# Revit family: LUXI_DOWNLIGHT_OD-E
name_source: partatom
category: Apparecchi per illuminazione
revit_build: Autodesk Revit 2016 (Build: 20161004_0715(x64)
units: mm (PartAtom-declared; Revit-internal decimal feet)

## family parameters
Condiviso = No
Host = Superficie
Numero OmniClass = 23.80.70.00
Punto di calcolo locali = Sì
Quota connettore circolare = Usa diametro
Sorgente d'illuminazione = Sì
Taglio con vuoti quando caricato = No
Tipo di parte = Normale
Titolo OmniClass = Lighting

## types (8) — shared parameters
ANG1 = 50.00°
Angolo inclinazione = -90.00°
CRI = ≥80 (typ.)
Certifications = CE / RohS
Color = White
Descrizione = LED Downlight with integrated driver
Dust and water protection rating = IP 44 (front)
Energy class = A+
Ext. thickness = 2 mm  [stored 0.00656168 ft]
Filtro dei colori = 16777215
IFCExportAs = IfcLightFixtureType
Impact rating = IK06 (1 Joule)
Installation = Recessed
Lifetime = L70B50 30.000h
Light distribution = Downlight
Light source = LED SMD
Masterformat 2016 code = 26.50.00
Masterformat 2016 description = Lighting
Material 1 = Polycarbonate_White
Material 2 = Opal Technopolimer
Modello = OD-E Series | Downlight
Operating temperature = 0°C / +40°C
Optics = Metalized reflector, opal diffusing panel
Photobiological risk group = RG0
Power factor = ≥0,90 (typ.)
Power supply = Included, not dimmable
Produttore = Luxi Illuminazione S.r.l.
Prospetto di default = 2000 mm  [stored 6.56168 ft]
Protection class = II
Rated supply voltage = 220-240V AC / 50-60 Hz
Rendi la forma visibile nel rendering = No
Review = 3
Step MacAdam (SDCM) = <4
URL = https://www.luxi.lighting
Uniclass 2015 code = EF_70_80
Uniclass 2015 description = Lighting
Variazione temperatura colore lampada con luminosità attenuata = <Nessuno>
Warranty = 3 years

## per-type parameters (varying)
| type | Carico apparente | Code | Diameter | Emetti da diametro cerchio | File diagramma fotometrico | H | H_mid | H_quart | OFF1 | OFF2 | OFF3 | OFF4 | Recession | Size | Wattage | Weight |
| DLDE010100W830 | 10 VA | DLDE010100W830 | 113 mm  [stored 0.370735 ft] | 100 mm  [stored 0.328084 ft] | DLDE010100W830 Luxi Serie OD-E 10W 3000K.IES | 59 mm | 30 mm  [stored 0.0984252 ft] | 15 mm | 25 mm  [stored 0.082021 ft] | 10 mm  [stored 0.0328084 ft] | 7 mm  [stored 0.0229659 ft] | 7 mm  [stored 0.0229659 ft] | 100 mm  [stored 0.328084 ft] | Ø113x59 recession Ø100 | 10 W | 0.30 kg |
| DLDE010100W840 | 10 VA | DLDE010100W840 | 113 mm  [stored 0.370735 ft] | 100 mm  [stored 0.328084 ft] | DLDE010100W840 Luxi Serie OD-E 10W 4000K.IES | 59 mm | 30 mm  [stored 0.0984252 ft] | 15 mm | 25 mm  [stored 0.082021 ft] | 10 mm  [stored 0.0328084 ft] | 7 mm  [stored 0.0229659 ft] | 7 mm  [stored 0.0229659 ft] | 100 mm  [stored 0.328084 ft] | Ø113x59 recession Ø100 | 10 W | 0.30 kg |
| DLDE017150W830 | 17 VA | DLDE017150W830 | 174 mm  [stored 0.570866 ft] | 150 mm  [stored 0.492126 ft] | DLDE017150W830 Luxi Serie OD-E 17W 3000K.IES | 66 mm  [stored 0.216535 ft] | 33 mm  [stored 0.108268 ft] | 17 mm | 28 mm | 11 mm | 8 mm  [stored 0.0262467 ft] | 12 mm  [stored 0.0393701 ft] | 150 mm  [stored 0.492126 ft] | Ø174x66 recession Ø150 | 17 W | 0.30 kg |
| DLDE017150W840 | 17 VA | DLDE017150W830 | 174 mm  [stored 0.570866 ft] | 150 mm  [stored 0.492126 ft] | DLDE017150W840 Luxi Serie OD-E 17W 4000K.IES | 66 mm  [stored 0.216535 ft] | 33 mm  [stored 0.108268 ft] | 17 mm | 28 mm | 11 mm | 8 mm  [stored 0.0262467 ft] | 12 mm  [stored 0.0393701 ft] | 150 mm  [stored 0.492126 ft] | Ø174x66 recession Ø150 | 17 W | 0.30 kg |
| DLDE025200W830 | 25 VA | DLDE025200W830 | 224 mm  [stored 0.734908 ft] | 200 mm  [stored 0.656168 ft] | DLDE025200W830 Luxi Serie OD-E 25W 3000K.IES | 85 mm  [stored 0.278871 ft] | 43 mm | 21 mm | 36 mm | 14 mm  [stored 0.0459318 ft] | 11 mm | 12 mm  [stored 0.0393701 ft] | 200 mm  [stored 0.656168 ft] | Ø224x85 recession Ø200 | 25 W | 0.50 kg |
| DLDE025200W840 | 25 VA | DLDE025200W840 | 224 mm  [stored 0.734908 ft] | 200 mm  [stored 0.656168 ft] | DLDE025200W840 Luxi Serie OD-E 25W 4000K.IES | 85 mm  [stored 0.278871 ft] | 43 mm | 21 mm | 36 mm | 14 mm  [stored 0.0459318 ft] | 11 mm | 12 mm  [stored 0.0393701 ft] | 200 mm  [stored 0.656168 ft] | Ø224x85 recession Ø200 | 25 W | 0.50 kg |
| DLDE035240W830 | 35 VA | DLDE035240W830 | 279 mm | 240 mm  [stored 0.787402 ft] | DLDE035240W830 Luxi Serie OD-E 35W 3000K.IES | 119 mm  [stored 0.39042 ft] | 60 mm | 30 mm  [stored 0.0984252 ft] | 50 mm  [stored 0.164042 ft] | 20 mm | 15 mm | 20 mm | 240 mm  [stored 0.787402 ft] | Ø279x119 recession Ø240 | 35 W | 0.60 kg |
| DLDE035240W840 | 35 VA | DLDE035240W840 | 279 mm | 240 mm  [stored 0.787402 ft] | DLDE035240W840 Luxi Serie OD-E 35W 4000K.IES | 119 mm  [stored 0.39042 ft] | 60 mm | 30 mm  [stored 0.0984252 ft] | 50 mm  [stored 0.164042 ft] | 20 mm | 15 mm | 20 mm | 240 mm  [stored 0.787402 ft] | Ø279x119 recession Ø240 | 35 W | 0.60 kg |

note: [stored X ft] marks values corroborated as IEEE doubles in the binary element streams (Revit-internal decimal feet)
